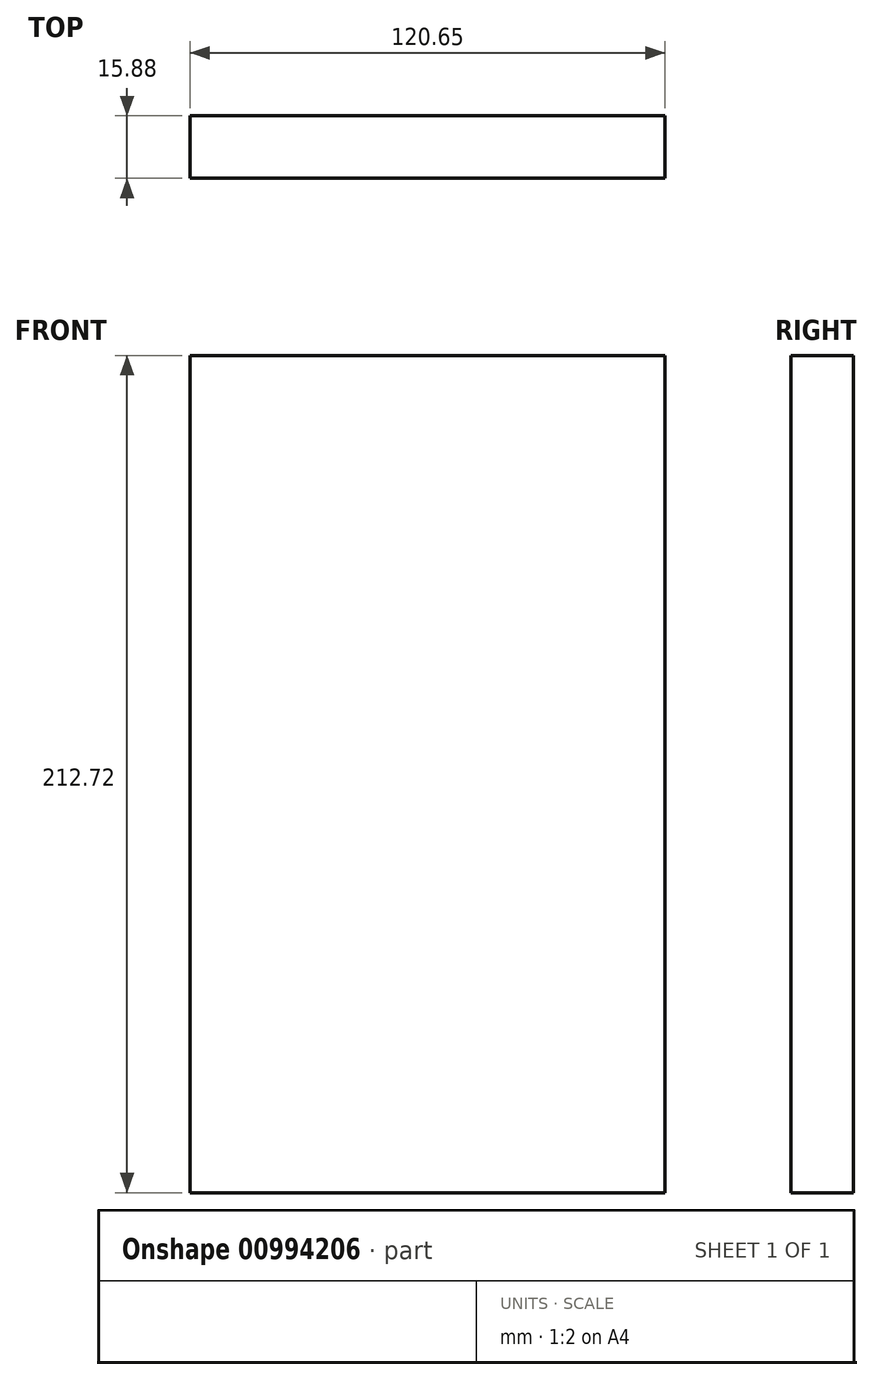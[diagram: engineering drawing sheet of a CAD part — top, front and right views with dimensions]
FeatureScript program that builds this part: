
annotation { "Feature Type Name" : "Feature", "Feature Type Description" : "" }
export const myFeature = defineFeature(function(context is Context, id is Id, definition is map)
    precondition{}
    {
        {
            var Q0;
            Q0=qCreatedBy(makeId("Front.planeOp"),FACE);
            var sketch = newSketch(context, id + "F0", { "sketchPlane" : qUnion([Q0])});
            skLineSegment(sketch, "E0.bottom", {"start": v(0, 0) * mm, "end": v(120.65, 0) * mm});
            skLineSegment(sketch, "E0.top", {"start": v(0, 212.73) * mm, "end": v(120.65, 212.73) * mm});
            skLineSegment(sketch, "E0.left", {"start": v(0, 0) * mm, "end": v(0, 212.72) * mm});
            skLineSegment(sketch, "E0.right", {"start": v(120.65, 0) * mm, "end": v(120.65, 212.72) * mm});
            skSolve(sketch);
        }
        {
            var Q0;
            Q0 = qSketchRegion(id + "F0", true);
            extrude(context, id + "F1", {"entities" : qUnion([Q0]), "depth" : 15.88 * mm, "offsetDistance" : 25.4 * mm});
        }
    });
